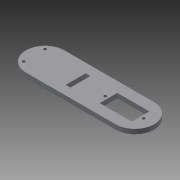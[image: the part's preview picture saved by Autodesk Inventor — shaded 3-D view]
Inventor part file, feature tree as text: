
AUTODESK INVENTOR PART (.ipt)
format: ipt  version: 2013 (Build 170138000, 138)  size: 114,176 bytes
history: native  units: mm
features: other x3, extrude x1, sketch x1
ambient origin geometry x8: Origin, YZ Plane, XZ Plane, XY Plane, X Axis, Y Axis, Z Axis, Center Point
feature tree (5):
  other  "Blocks"
  extrude  "Extrusion4"  Depth=3.0mm
  sketch  "Sketch1"  dims[d0=3.0mm d2=3.0mm d3=0.1mm d7=22.5mm d8=12.4mm d9=4.5mm d10=4.5mm d11=2.0mm d12=2.0mm d23=90.0mm d24=27.0mm d25=5.0mm d26=2.0mm d27=5.0mm d28=5.0mm d29=3.25mm d30=14.0mm d31=35.0mm d36=13.0mm d38=13.0mm d40=3.25mm d41=0.0mm]
  other  "Block1"
  other  "Block1:1"
